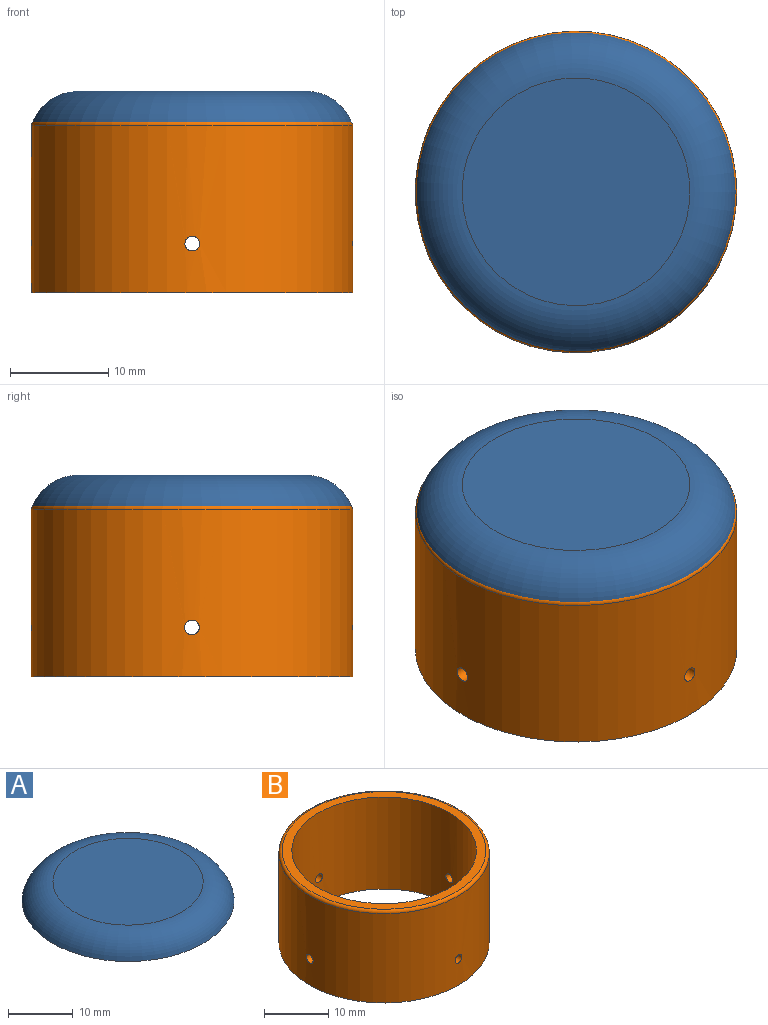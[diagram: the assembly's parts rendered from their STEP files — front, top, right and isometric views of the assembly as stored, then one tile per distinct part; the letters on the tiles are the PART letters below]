
ASSEMBLY  parts=2 mates=1
PART A: 5 faces, bbox 35.9x35.9x5 mm
  f0: plane 32.7x32.7mm, normal (0,0,-1), area 177.5mm2, adj f2,f4
  f1: plane 23.16x23.16mm, normal (0,0,1), area 421.3mm2, adj f2
  f2: torus R=11.58mm, axis (0,0,-1), area 570.6mm2, adj f0,f1
  f3: plane 23.16x23.16mm, normal (0,0,-1), area 421.3mm2, adj f4
  f4: torus R=11.58mm, axis (0,0,-1), area 301.2mm2, adj f0,f3
PART B: 9 faces, bbox 35.4x35.4x17.5 mm
  f0: cylinder r=14.35mm len=28.7mm, axis (0,0,-1), area 1570.8mm2, adj f2,f3,f4,f5,f6,f7
  f1: cylinder r=16.35mm len=32.7mm, axis (0,0,-1), area 1739.3mm2, adj f3,f4,f5,f6,f7,f8
  f2: plane 31.7x31.7mm, normal (0,0,1), area 142.3mm2, adj f0,f8
  f3: plane 32.7x32.7mm, normal (0,0,-1), area 192.9mm2, adj f0,f1
  f4: cylinder r=0.75mm len=2.02mm, axis (1,0,0), area 9.4mm2, adj f0,f1
  f5: cylinder r=0.75mm len=2.02mm, axis (1,0,0), area 9.4mm2, adj f0,f1
  f6: cylinder r=0.75mm len=2.02mm, axis (0,-1,0), area 9.4mm2, adj f0,f1
  f7: cylinder r=0.75mm len=2.02mm, axis (0,-1,0), area 9.4mm2, adj f0,f1
  f8: torus R=15.85mm, axis (0,0,1), area 79.8mm2, adj f1,f2
PLACE A t=(-5.34,-4.27,23.08)mm
PLACE B t=(-5.34,-4.27,2.58)mm
MATE fastened B.f1 <-> A.f2  axis (0,0,-1) through (-5.34,-4.27,19.58)mm
